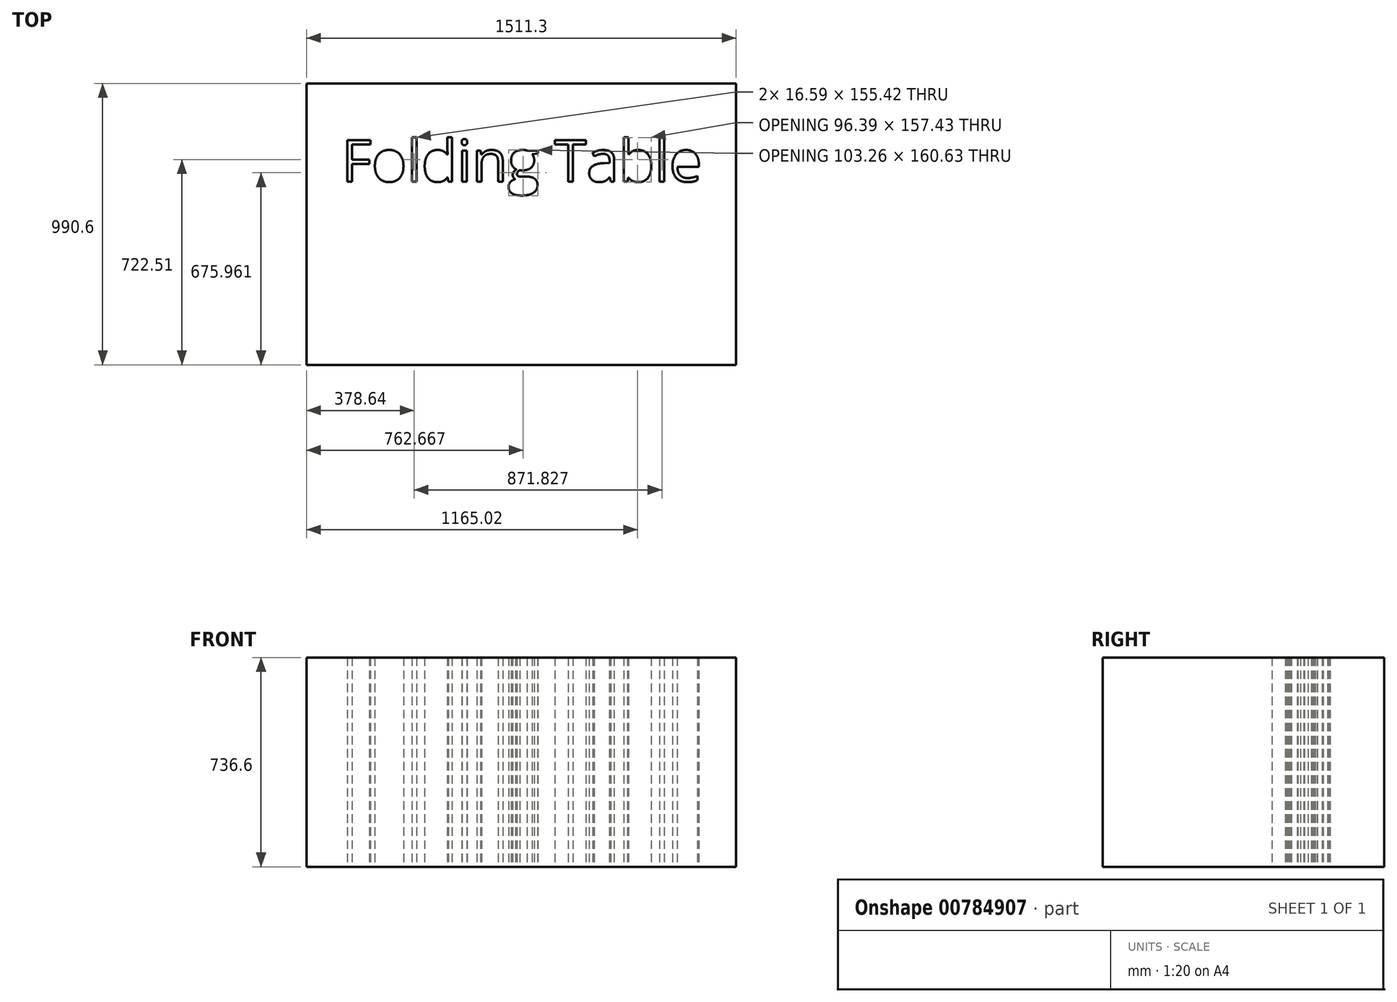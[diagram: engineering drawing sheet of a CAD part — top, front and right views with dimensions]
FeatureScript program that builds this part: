
annotation { "Feature Type Name" : "Feature", "Feature Type Description" : "" }
export const myFeature = defineFeature(function(context is Context, id is Id, definition is map)
    precondition{}
    {
        {
            var Q0;
            Q0=qCreatedBy(makeId("Top.planeOp"),FACE);
            var sketch = newSketch(context, id + "F0", { "sketchPlane" : qUnion([Q0])});
            skLineSegment(sketch, "E0.bottom", {"start": v(755.65, 495.3) * mm, "end": v(-755.65, 495.3) * mm});
            skLineSegment(sketch, "E0.top", {"start": v(755.65, -495.3) * mm, "end": v(-755.65, -495.3) * mm});
            skLineSegment(sketch, "E0.left", {"start": v(755.65, 495.3) * mm, "end": v(755.65, -495.3) * mm});
            skLineSegment(sketch, "E0.right", {"start": v(-755.65, 495.3) * mm, "end": v(-755.65, -495.3) * mm});
            skPoint(sketch, "E0.middle", {"position": v(0, 0) * mm});
            skText(sketch, "E1", { "text": "Folding Table", "fontName": "OpenSans-Regular.ttf"});
            const initialGuessF0  = {"E1": [-0.632, 0.1495, 1, 0, 0.14727]};
            skSetInitialGuess(sketch, initialGuessF0);
            skSolve(sketch);
        }
        {
            var Q0;
            Q0=makeQuery(id+"F0.imprint","IMPRINT",FACE,{"disambiguationData":[TD([[makeQuery(id+"F0.imprint","IMPRINT",EDGE,{"derivedFrom":sQuery(id+"F0.wireOp",EDGE,"E0.bottom")}),1.0]])]});
            extrude(context, id + "F1", {"entities" : qUnion([Q0]), "depth" : 736.6 * mm, "offsetDistance" : 25.4 * mm});
        }
    });
